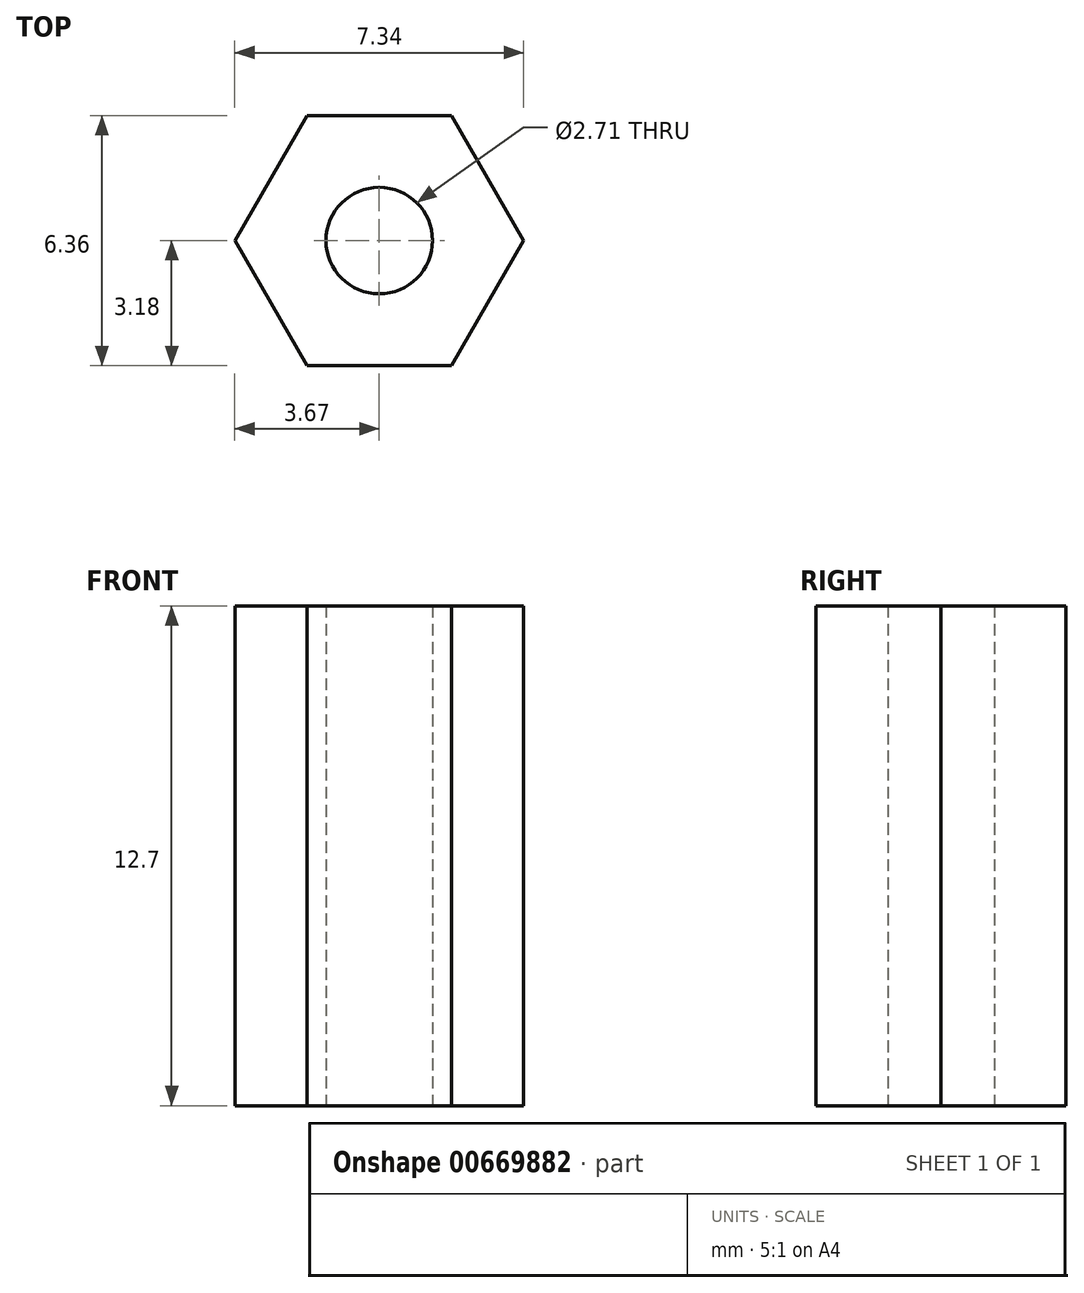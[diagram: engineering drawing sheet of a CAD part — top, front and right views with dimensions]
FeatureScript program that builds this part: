
annotation { "Feature Type Name" : "Feature", "Feature Type Description" : "" }
export const myFeature = defineFeature(function(context is Context, id is Id, definition is map)
    precondition{}
    {
        {
            var Q0;
            Q0=qCreatedBy(makeId("Top.planeOp"),FACE);
            var sketch = newSketch(context, id + "F0", { "sketchPlane" : qUnion([Q0])});
            skCircle(sketch, "E0.cCircle", {"center": v(0, 0) * mm, "radius": 3.18 * mm, "construction": true});
            skLineSegment(sketch, "E0.0", {"start": v(3.67, 0) * mm, "end": v(1.83, -3.18) * mm});
            skLineSegment(sketch, "E0.1", {"start": v(1.83, -3.18) * mm, "end": v(-1.83, -3.18) * mm});
            skLineSegment(sketch, "E0.2", {"start": v(-1.83, -3.18) * mm, "end": v(-3.67, 0) * mm});
            skLineSegment(sketch, "E0.3", {"start": v(-3.67, 0) * mm, "end": v(-1.83, 3.17) * mm});
            skLineSegment(sketch, "E0.4", {"start": v(-1.83, 3.18) * mm, "end": v(1.83, 3.18) * mm});
            skLineSegment(sketch, "E0.5", {"start": v(1.83, 3.18) * mm, "end": v(3.67, 0) * mm});
            skPoint(sketch, "E0.0.midPoint", {"position": v(3.18, 0) * mm});
            skSolve(sketch);
        }
        {
            var Q0;
            Q0=qSketchRegion(id+"F0",true);
            extrude(context, id + "F1", {"entities" : qUnion([Q0]), "depth" : 12.7 * mm});
        }
        {
            var Q0;
            Q0=makeQuery(id+"F1.opExtrude","CAP_FACE",FACE,{"disambiguationData":[OSD([sQuery(id+"F0.wireOp",EDGE,"E0.0"),sQuery(id+"F0.wireOp",EDGE,"E0.1"),sQuery(id+"F0.wireOp",EDGE,"E0.2"),sQuery(id+"F0.wireOp",EDGE,"E0.3"),sQuery(id+"F0.wireOp",EDGE,"E0.4"),sQuery(id+"F0.wireOp",EDGE,"E0.5")])],"isStart":false});
            var sketch = newSketch(context, id + "F2", { "sketchPlane" : qUnion([Q0])});
            skPoint(sketch, "E1", {"position": v(0, 0) * mm});
            skSolve(sketch);
        }
        {
            var Q0;
            Q0=sQuery(id+"F2.wireOp",VERTEX,"E1");
            var Q1;
            Q1=makeQuery(id+"F1.opExtrude","SWEPT_BODY",BODY,{"disambiguationData":[OSD([sQuery(id+"F0.wireOp",EDGE,"E0.0"),sQuery(id+"F0.wireOp",EDGE,"E0.1"),sQuery(id+"F0.wireOp",EDGE,"E0.2"),sQuery(id+"F0.wireOp",EDGE,"E0.3"),sQuery(id+"F0.wireOp",EDGE,"E0.4"),sQuery(id+"F0.wireOp",EDGE,"E0.5")])]});
            hole(context, id + "F3", {"style" : HoleStyle.SIMPLE, "endStyle" : HoleEndStyle.THROUGH, "standardTappedOrClearance" : lookupTablePath({ "standard" : "ANSI", "engagement" : "75%", "pitch" : "32 tpi", "size" : "#6", "type" : "Tapped" }), "standardBlindInLast" : lookupTablePath({ "standard" : "ANSI", "engagement" : "75%", "pitch" : "32 tpi", "size" : "#6", "type" : "Tapped" }), "holeDiameter" : 2.7 * mm, "showTappedDepth" : true, "tappedDepth" : 2.77 * mm, "tapClearance" : 3, "startFromSketch" : true, "locations" : qUnion([Q0]), "scope" : qUnion([Q1]), "majorDiameter" : 3.5 * mm});
        }
    });
